# Revit family: Lighting-Industrial-GEWISS-SMART[4]HE_HIGHBAYS-LED_EMERGENCY_2M
name_source: partatom
category: Apparecchi per illuminazione
units: mm (PartAtom-declared; Revit-internal decimal feet)

## family parameters
Basato su piano di lavoro = Sì
Condiviso = No
Numero OmniClass = 23.80.70.11.21
Punto di calcolo locali = No
Quota connettore circolare = Usa diametro
Sempre verticale = No
Sorgente d'illuminazione = No
Taglio con vuoti quando caricato = No
Tipo di parte = Normale
Titolo OmniClass = Emergency Lighting

## types (18) — shared parameters
Application = Internal
Body = PA6 "Halogen Free" loaded fibreglass
Carico apparente = 100 VA
Catalogue = LIGHTING
Classification: = -
Classificazione = Lighting
Color Rendering Index = CRI-80
Colour = Grey RAL 7035
Colour : = Grey RAL 7035
Context = Lighting for industries and sports facilities
Control System = 1 x DALI DT6 + 1 x DALI DT1 (Emerg. 3h)
DIN 18032-3 certification = -
Device with reduced surface temperature = Yes
Dist_sorg_lum = 10 mm  [stored 0.0328084 ft]
Driver = Included
Driver Box = Built-in
Electrocod = 2444
Eletrical and lighting features = -
External screw = Stainless steel
Fixing = -
Gasket = anti-aging silicone
General information = -
Glow Wire Test : = 850 °C
IDF = 771d9fb1-981c-42ae-aedb-5e9a004f6ebe
IDT = 91df4c41cb4c4ac4b5ce1e3797edda73
IP degree = IP65
IPEA = -
Immagine tipo = GWL1391E.jpg
Installationa and maintenance = -
Insulation class = I
LED Maintenance = NiMh Battery Only
Lampada = LED
Larghezza = 254 mm
Lifetime = L90B10 (Tq+25°C) = 100.000 h - L90B10 (Tq+50°C) = 50.000 h
Locking Hook = -
Luminaire = LED Industrial ReflectorÂ
Lunghezza = 699 mm  [stored 2.29331 ft]
Mascherina = <Per categoria>
Materials = -
Maximum surface exposed to the wind : = 0,220 m²
Motore = <Per categoria>
Mouting and installation = Ceiling light - Suspension
Operating temperature : = 0 ÷ +40 °C
Optic Maintenance = Non-replaceable
Optic and illuminating features = -
Overvoltage protection = DM 6 kV / CM 10 kV
Photobiological Risk Class = RG0
Produttore = GEWISS S.p.A.
Prospetto di default = 1219 mm
Rated frequency (Hz) = 50/60 Hz
Shield type = Tempered glass Thickness 4mm
Shock resistance = IK08
Spessore plafoniera = 40 mm  [stored 0.131234 ft]
Standard Deviation Colour Matching = SDCM = 3
Standard- = EN 60598-2-22 ; EN 60598-1 ; EN 60598-2-24
Standards and approvals = -
Stocking temperature = -40 +70 °C
Struttura plafoniera = <Per categoria>
Supply voltage = 220 - 240 V
System power : = 95 W (+5W Emerg.)
Technical sheet = https://www.gewiss.com
Tilt- = -
Trasformatore = <Per categoria>
Type of light source = LED - Not replaceable
URL = https://www.gewiss.com
Unique digital code (Datamatrix) = Datamatrix
Version file RFA = 20.11
Voltaggio = 230 V
Warranty = 5 years
Weight (kg): = 8
Wiring = With GW connect watertight connector

## per-type parameters (varying)
| type | Colour temperature | Descrizione | Efficiency (lm/W) | Lumen output (lm) : | Modello | Optic | Optic : | Unified Glare Rating |
| GWS4224AA857 - SMART4HB 2M EMERG ARR.57K | 5700K | SMART[4]HB 2M EMERG ARR.57K | 138 | 13800 (850 Emerg.) | GWS4224AA857 | Array | Metallized polycarbonate reflector | UGR - 25 |
| GWS4224AA840 - SMART4HB 2M EMERG ARR.40K | 4000K | SMART[4]HB 2M EMERG ARR.40K | 138 | 13800 (850 Emerg.) | GWS4224AA840 | Array | Metallized polycarbonate reflector | UGR - 25 |
| GWS4224AQ857 - SMART4HB 2M EMERG ELL.57K | 5700K | SMART[4]HB 2M EMERG ELL.57K | 123 | 12300 (750 Emerg.) | GWS4224AQ857 | Elliptical | Metallic PC reflector and PMMA lenses | - |
| GWS4224AH857 - SMART4HB 2M EMERG 60° 57K | 5700K | SMART[4]HB 2M EMERG 60° 57K | 138 | 13800 (850 Emerg.) | GWS4224AH857 | 60° | Metallic PC reflector and PMMA lenses | UGR - 22 |
| GWS4224AC830 - SMART4HB 2M EMERG ASI.30K | 3000K | SMART[4]HB 2M EMERG ASI.30K | 119 | 11900 (710 Emerg.) | GWS4224AC830 | Asymmetrical | Metallic PC reflector and PMMA lenses | - |
| GWS4224AF840 - SMART4HB 2M EMERG 30° 40K | 4000K | SMART[4]HB 2M EMERG 30° 40K | 137 | 13700 (850 Emerg.) | GWS4224AF840 | 30° | Metallic PC reflector and PMMA lenses | UGR - 19 |
| GWS4224AA830 - SMART4HB 2M EMERG ARR.30K | 3000K | SMART[4]HB 2M EMERG ARR.30K | 132 | 13200 (810 Emerg.) | GWS4224AA830 | Array | Metallized polycarbonate reflector | UGR - 25 |
| GWS4224AQ840 - SMART4HB 2M EMERG ELL.40K | 4000K | SMART[4]HB 2M EMERG ELL.40K | 123 | 12300 (750 Emerg.) | GWS4224AQ840 | Elliptical | Metallic PC reflector and PMMA lenses | - |
| GWS4224AQ830 - SMART4HB 2M EMERG ELL.30K | 3000K | SMART[4]HB 2M EMERG ELL.30K | 118 | 11800 (710 Emerg.) | GWS4224AQ830 | Elliptical | Metallic PC reflector and PMMA lenses | - |
| GWS4224AH840 - SMART4HB 2M EMERG 60° 40K | 4000K | SMART[4]HB 2M EMERG 60° 40K | 138 | 13800 (850 Emerg.) | GWS4224AH840 | 60° | Metallic PC reflector and PMMA lenses | UGR - 22 |
| GWS4224AH830 - SMART4HB 2M EMERG 60° 30K | 3000K | SMART[4]HB 2M EMERG 60° 30K | 131 | 13100 (810 Emerg.) | GWS4224AH830 | 60° | Metallic PC reflector and PMMA lenses | UGR - 22 |
| GWS4224AP830 - SMART4HB 2M EMERG 90° 30K | 3000K | SMART[4]HB 2M EMERG 90° 30K | 133 | 13300 (810 Emerg.) | GWS4224AP830 | 90° | Metallic PC reflector and PMMA lenses | UGR - 22 |
| GWS4224AC857 - SMART4HB 2M EMERG ASI.57K | 5700K | SMART[4]HB 2M EMERG ASI.57K | 125 | 12500 (750 Emerg.) | GWS4224AC857 | Asymmetrical | Metallic PC reflector and PMMA lenses | - |
| GWS4224AP840 - SMART4HB 2M EMERG 90° 40K | 4000K | SMART[4]HB 2M EMERG 90° 40K | 139 | 13900 (850 Emerg.) | GWS4224AP840 | 90° | Metallic PC reflector and PMMA lenses | UGR - 22 |
| GWS4224AF830 - SMART4HB 2M EMERG 30° 30K | 3000K | SMART[4]HB 2M EMERG 30° 30K | 130 | 13000 (810 Emerg.) | GWS4224AF830 | 30° | Metallic PC reflector and PMMA lenses | UGR - 19 |
| GWS4224AC840 - SMART4HB 2M EMERG ASI.40K | 4000K | SMART[4]HB 2M EMERG ASI.40K | 125 | 12500 (750 Emerg.) | GWS4224AC840 | Asymmetrical | Metallic PC reflector and PMMA lenses | - |
| GWS4224AP857 - SMART4HB 2M EMERG 90° 57K | 5700K | SMART[4]HB 2M EMERG 90° 57K | 139 | 13900 (850 Emerg.) | GWS4224AP857 | 90° | Metallic PC reflector and PMMA lenses | UGR - 22 |
| GWS4224AF857 - SMART4HB 2M EMERG 30° 57K | 5700K | SMART[4]HB 2M EMERG 30° 57K | 137 | 13700 (850 Emerg.) | GWS4224AF857 | 30° | Metallic PC reflector and PMMA lenses | UGR - 19 |

note: [stored X ft] marks values corroborated as IEEE doubles in the binary element streams (Revit-internal decimal feet)

## geometry (parser evidence)
native form markers: Blend x2, Sweep x1
no freeform markers — native parametric forms only
